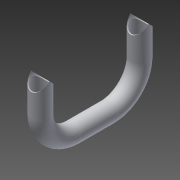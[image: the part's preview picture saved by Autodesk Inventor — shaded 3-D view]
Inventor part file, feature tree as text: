
AUTODESK INVENTOR PART (.ipt)
format: ipt  version: 2015 (Build 190159000, 159)  size: 182,784 bytes
history: native  units: mm
features: other x5, sketch x3, sweep x1, extrude x1
ambient origin geometry x8: Origin, YZ Plane, XZ Plane, XY Plane, X Axis, Y Axis, Z Axis, Center Point
bodies: Body1 (feature_tree)
feature tree (10):
  other  "Bryła1"
  other  "Płaszczyzna konstrukcyjna1"
  sketch  "Szkic1"
  other  "Płaszczyzna konstrukcyjna2"
  sweep  "Przeciągnięcie1"
  extrude  "Wyciągnięcie proste1"  Depth=1.5mm
  other  "Utwórz kombinację1"
  sketch  "Szkic2"
  sketch  "Szkic3"
  other  "Bryła2"
